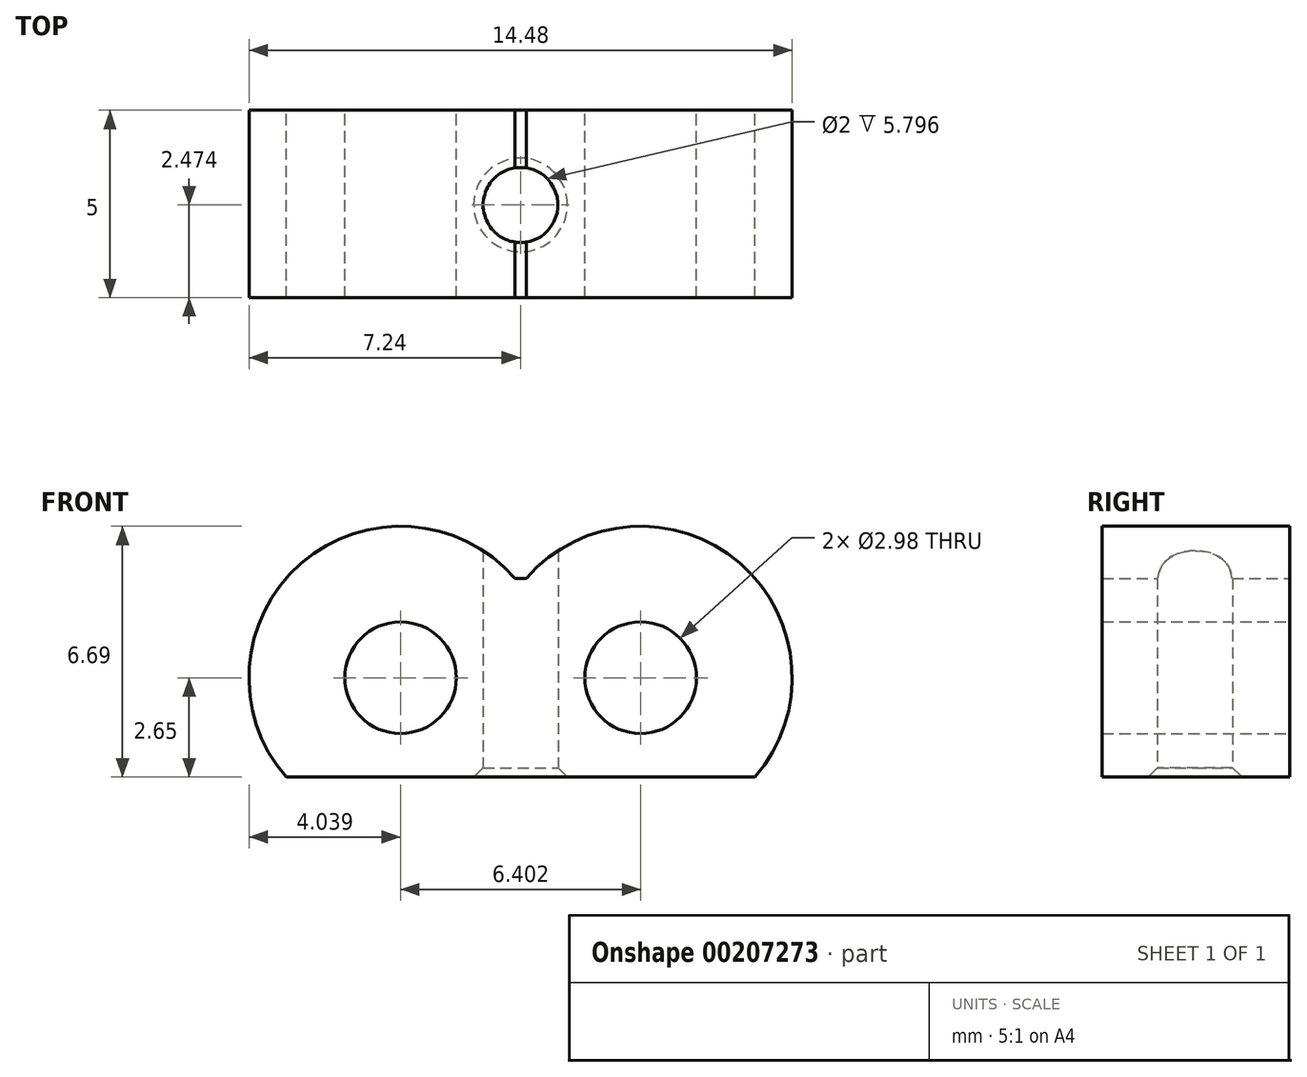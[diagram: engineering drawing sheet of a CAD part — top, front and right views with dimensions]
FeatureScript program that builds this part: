
annotation { "Feature Type Name" : "Feature", "Feature Type Description" : "" }
export const myFeature = defineFeature(function(context is Context, id is Id, definition is map)
    precondition{}
    {
        {
            var Q0;
            Q0=qCreatedBy(makeId("Front.planeOp"),FACE);
            var sketch = newSketch(context, id + "F0", { "sketchPlane" : qUnion([Q0])});
            skLineSegment(sketch, "E0.bottom", {"start": v(6.25, -2.65) * mm, "end": v(-6.25, -2.65) * mm});
            skLineSegment(sketch, "E0.top", {"start": v(0.15, 2.65) * mm, "end": v(-0.15, 2.65) * mm});
            skPoint(sketch, "E0.middle", {"position": v(0, 0) * mm});
            skLineSegment(sketch, "E1", {"start": v(0, -2.47) * mm, "end": v(0, 0) * mm, "construction": true});
            skPoint(sketch, "E1.endSnap0", {"position": v(0, -2.65) * mm});
            skLineSegment(sketch, "E2", {"start": v(0, 0) * mm, "end": v(15.5, 0) * mm, "construction": true});
            skLineSegment(sketch, "E3.trimOffspring", {"start": v(0, 2.47) * mm, "end": v(0, 14.8) * mm, "construction": true});
            skArc(sketch, "E4.trimOffspring", {"start": v(6.25, -2.65) * mm, "mid": v(5.85, 3.05) * mm, "end": v(0.15, 2.65) * mm});
            skPoint(sketch, "E5.center.orphan", {"position": v(6.25, 0) * mm});
            skArc(sketch, "E6.MirrorCS", {"start": v(-6.25, -2.65) * mm, "mid": v(-5.85, 3.05) * mm, "end": v(-0.15, 2.65) * mm});
            skPoint(sketch, "E0.right.end.orphan", {"position": v(-6.25, 2.65) * mm});
            skLineSegment(sketch, "E7", {"start": v(0, -2.47) * mm, "end": v(0, 2.47) * mm});
            skCircle(sketch, "E8", {"center": v(3.2, 0) * mm, "radius": 1.49 * mm});
            skCircle(sketch, "E9.MirrorC", {"center": v(-3.2, 0) * mm, "radius": 1.49 * mm});
            skPoint(sketch, "E0.left.end.orphan", {"position": v(6.25, 2.65) * mm});
            skSolve(sketch);
        }
        {
            var Q0;
            Q0=makeQuery(id+"F0.imprint","IMPRINT",FACE,{"disambiguationData":[TD([[makeQuery(id+"F0.imprint","IMPRINT",EDGE,{"derivedFrom":sQuery(id+"F0.wireOp",EDGE,"E0.bottom")}),-1.0]])]});
            extrude(context, id + "F1", {"entities" : qUnion([Q0]), "depth" : 5 * mm});
        }
        {
            var Q0;
            Q0=qCreatedBy(makeId("Front.planeOp"),FACE);
            var sketch = newSketch(context, id + "F2", { "sketchPlane" : qUnion([Q0])});
            skPoint(sketch, "E10", {"position": v(-2.73, 22.6) * mm});
            skSolve(sketch);
        }
        {
            var Q0;
            Q0=sQuery(id+"F2.wireOp",VERTEX,"E10");
            var Q1;
            Q1=makeQuery(id+"F1.opExtrude","SWEPT_BODY",BODY,{"disambiguationData":[OSD([sQuery(id+"F0.wireOp",EDGE,"E0.bottom"),sQuery(id+"F0.wireOp",EDGE,"E0.top"),sQuery(id+"F0.wireOp",EDGE,"E4.trimOffspring"),sQuery(id+"F0.wireOp",EDGE,"E6.MirrorCS"),sQuery(id+"F0.wireOp",EDGE,"E8"),sQuery(id+"F0.wireOp",EDGE,"E9.MirrorC")])]});
            hole(context, id + "F3", {"style" : HoleStyle.C_SINK, "endStyle" : HoleEndStyle.THROUGH, "standardTappedOrClearance" : lookupTablePath({ "standard" : "ISO", "fit" : "Normal", "size" : "M5", "type" : "Clearance" }), "standardBlindInLast" : lookupTablePath({ "fit" : "Standard", "standard" : "ISO", "size" : "M5", "type" : "Clearance" }), "holeDiameter" : 5.5 * mm, "cSinkDiameter" : 11.2 * mm, "cSinkAngle" : 90 * degree, "startFromSketch" : true, "locations" : qUnion([Q0]), "scope" : qUnion([Q1]), "isTappedThrough" : true});
        }
        {
            var Q0;
            Q0=makeQuery(id+"F1.opExtrude","SWEPT_FACE",FACE,{"disambiguationData":[OSD([sQuery(id+"F0.wireOp",EDGE,"E0.bottom")])]});
            var sketch = newSketch(context, id + "F4", { "sketchPlane" : qUnion([Q0])});
            skPoint(sketch, "E11", {"position": v(0, 2.53) * mm});
            skSolve(sketch);
        }
        {
            var Q0;
            Q0=sQuery(id+"F4.wireOp",VERTEX,"E11");
            var Q1;
            Q1=makeQuery(id+"F1.opExtrude","SWEPT_BODY",BODY,{"disambiguationData":[OSD([sQuery(id+"F0.wireOp",EDGE,"E0.bottom"),sQuery(id+"F0.wireOp",EDGE,"E0.top"),sQuery(id+"F0.wireOp",EDGE,"E4.trimOffspring"),sQuery(id+"F0.wireOp",EDGE,"E6.MirrorCS"),sQuery(id+"F0.wireOp",EDGE,"E8"),sQuery(id+"F0.wireOp",EDGE,"E9.MirrorC")])]});
            hole(context, id + "F5", {"style" : HoleStyle.C_SINK, "endStyle" : HoleEndStyle.THROUGH, "holeDiameter" : 2 * mm, "cSinkDiameter" : 2.5 * mm, "cSinkAngle" : 90 * degree, "locations" : qUnion([Q0]), "scope" : qUnion([Q1]), "isTappedThrough" : true});
        }
    });
